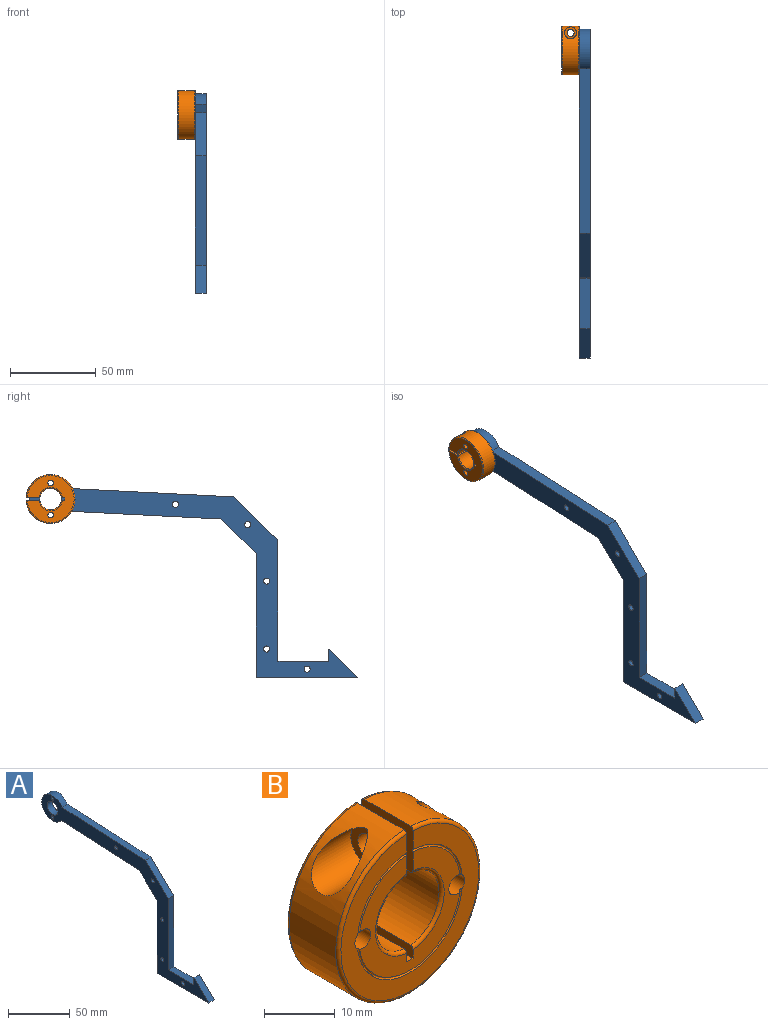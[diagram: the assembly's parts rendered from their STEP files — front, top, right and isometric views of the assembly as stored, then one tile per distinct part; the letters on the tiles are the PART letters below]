
ASSEMBLY  parts=2 mates=1
PART A: 21 faces, bbox 6.4x192x116.6 mm
  f0: cylinder r=12.44mm len=24.88mm, axis (-1,0,0), area 407.3mm2, adj f1,f10,f12,f13
  f1: plane 96.11x6.35mm, normal (0,-0.05,1), area 611.1mm2, adj f0,f2,f12,f13
  f2: plane 25.97x25.14mm, normal (0,-0.7,0.72), area 229.5mm2, adj f1,f3,f12,f13
  f3: plane 70.79x6.35mm, normal (0,-1,0), area 449.5mm2, adj f2,f4,f12,f13
  f4: plane 29.53x6.35mm, normal (0,0,1), area 187.5mm2, adj f3,f5,f12,f13
  f5: plane 7.04x6.35mm, normal (0,1,0), area 44.7mm2, adj f4,f6,f12,f13
  f6: plane 17.13x16.56mm, normal (0,-0.7,0.72), area 151.3mm2, adj f5,f7,f12,f13
  f7: plane 59.36x6.35mm, normal (0,0,-1), area 376.9mm2, adj f6,f8,f12,f13
  f8: plane 72.39x6.35mm, normal (0,1,0), area 459.7mm2, adj f7,f9,f12,f13
  f9: plane 20.82x20.16mm, normal (0,0.7,-0.72), area 184mm2, adj f8,f10,f12,f13
  f10: plane 89.12x6.35mm, normal (0,0.05,-1), area 566.7mm2, adj f0,f9,f12,f13
  f11: cylinder r=6.35mm len=12.7mm, axis (-1,0,0), area 253.4mm2, adj f12,f13
  f12: plane 191.96x116.62mm, normal (1,0,0), area 3374.2mm2, adj f0,f1,f2,f3,f4,f5,f6,f7
  f13: plane 191.96x116.62mm, normal (-1,0,0), area 3374.2mm2, adj f0,f1,f2,f3,f4,f5,f6,f7
  f14: cylinder r=1.59mm len=6.35mm, axis (1,0,0), area 63.3mm2, adj f12,f13
  f15: cylinder r=1.59mm len=6.35mm, axis (1,0,0), area 63.3mm2, adj f12,f13
  f16: cylinder r=1.78mm len=6.35mm, axis (1,0,0), area 70.9mm2, adj f12,f13
  f17: cylinder r=1.78mm len=6.35mm, axis (1,0,0), area 70.9mm2, adj f12,f13
  f18: cylinder r=1.78mm len=6.35mm, axis (1,0,0), area 70.9mm2, adj f12,f13
  f19: cylinder r=1.78mm len=6.35mm, axis (1,0,0), area 70.9mm2, adj f12,f13
  f20: cylinder r=1.78mm len=6.35mm, axis (1,0,0), area 70.9mm2, adj f12,f13
PART B: 26 faces, bbox 30.9x10.5x30.9 mm
  f0: torus R=10.32mm, axis (0,1,0), area 8.5mm2, adj f4,f5,f11,f25
  f1: torus R=10.32mm, axis (0,1,0), area 8.5mm2, adj f2,f5,f11,f24
  f2: plane 10.34x7.97mm, normal (1,0,0), area 68.2mm2, adj f1,f3,f5,f9,f11,f12,f15,f16
  f3: cylinder r=14.29mm len=28.58mm, axis (0,1,0), area 741mm2, adj f2,f4,f15,f16,f20,f21
  f4: plane 10.34x7.97mm, normal (-1,0,0), area 68.2mm2, adj f0,f3,f5,f10,f11,f12,f13,f14
  f5: plane 27.54x27.53mm, normal (0,-1,0), area 243.1mm2, adj f0,f1,f2,f4,f15,f19,f24,f25
  f6: plane 10.34x2.04mm, normal (-1,0,0), area 20.7mm2, adj f7,f10,f11,f12,f13,f14
  f7: plane 10.32x1.27mm, normal (0,0,1), area 13.1mm2, adj f6,f8,f11,f12
  f8: plane 10.34x2.04mm, normal (1,0,0), area 20.7mm2, adj f7,f9,f11,f12,f17,f18
  f9: cylinder r=6.35mm len=12.64mm, axis (0,1,0), area 173.5mm2, adj f2,f8,f17,f18
  f10: cylinder r=6.35mm len=12.64mm, axis (0,1,0), area 173.5mm2, adj f4,f6,f13,f14
  f11: plane 20.24x20.05mm, normal (0,-1,0), area 155.9mm2, adj f0,f1,f2,f4,f6,f7,f8,f13
  f12: plane 27.54x27.53mm, normal (0,1,0), area 421.2mm2, adj f2,f4,f6,f7,f8,f14,f16,f18
  f13: torus R=6.87mm, axis (0,-1,0), area 15.6mm2, adj f4,f6,f10,f11
  f14: torus R=6.87mm, axis (0,-1,0), area 15.6mm2, adj f4,f6,f10,f12
  f15: torus R=13.77mm, axis (0,-1,0), area 70.8mm2, adj f2,f3,f4,f5
  f16: torus R=13.77mm, axis (0,-1,0), area 70.8mm2, adj f2,f3,f4,f12
  f17: torus R=6.87mm, axis (0,-1,0), area 15.6mm2, adj f2,f8,f9,f11
  f18: torus R=6.87mm, axis (0,-1,0), area 15.6mm2, adj f2,f8,f9,f12
  f19: torus R=10.32mm, axis (0,1,0), area 17.8mm2, adj f5,f11,f24,f25
  f20: cylinder r=2.08mm len=11.06mm, axis (1,0,0), area 118.2mm2, adj f3,f4
  f21: cylinder r=3.49mm len=9.44mm, axis (1,0,0), area 131.4mm2, adj f3,f23
  f22: cylinder r=2.08mm len=4.17mm, axis (1,0,0), area 32.6mm2, adj f2,f23
  f23: plane 6.99x6.99mm, normal (-1,0,0), area 24.7mm2, adj f21,f22
  f24: cylinder r=1.59mm len=10.32mm, axis (0,1,0), area 102.8mm2, adj f1,f5,f11,f12,f19
  f25: cylinder r=1.59mm len=10.32mm, axis (0,1,0), area 102.8mm2, adj f0,f5,f11,f12,f19
PLACE A t=(91.16,96.85,79.59)mm
PLACE B rot(axis=(-0.58,0.58,0.58),120deg) t=(86,140.85,46.9)mm
MATE fastened B.f0 <-> A.f0  axis (1,0,0) through (91.16,140.85,46.9)mm
